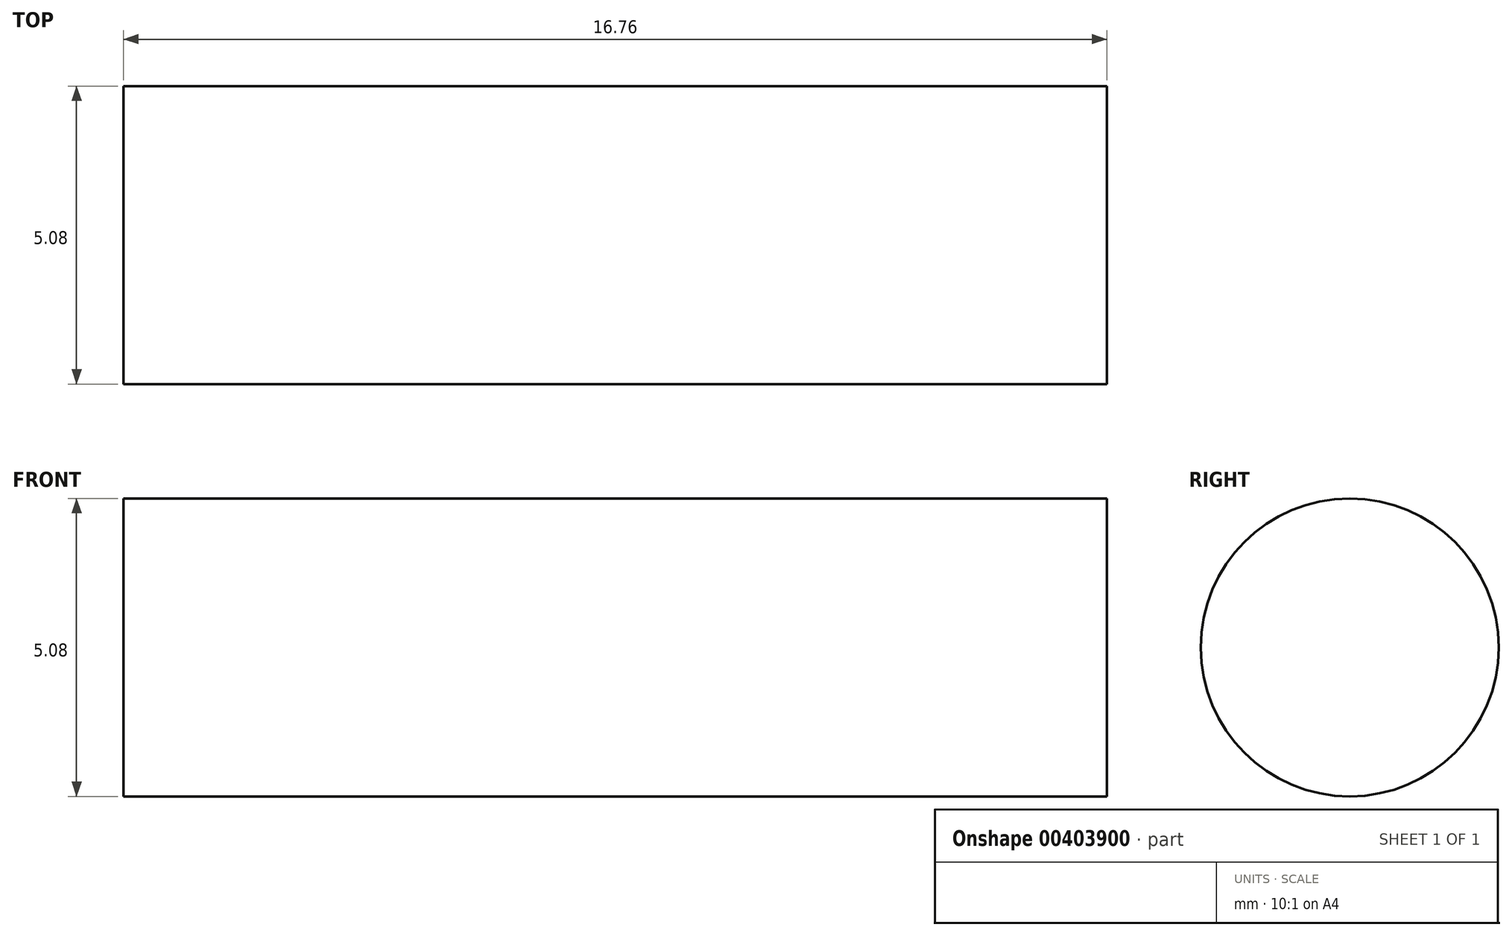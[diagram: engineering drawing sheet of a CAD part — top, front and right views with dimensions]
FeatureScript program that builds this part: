
annotation { "Feature Type Name" : "Feature", "Feature Type Description" : "" }
export const myFeature = defineFeature(function(context is Context, id is Id, definition is map)
    precondition{}
    {
        {
            var Q0;
            Q0=qCreatedBy(makeId("Right.planeOp"),FACE);
            var sketch = newSketch(context, id + "F0", { "sketchPlane" : qUnion([Q0])});
            skCircle(sketch, "E0", {"center": v(0, 0) * mm, "radius": 12.7 * mm});
            skSolve(sketch);
        }
        {
            var Q0;
            Q0=qSketchRegion(id+"F0",true);
            var Q1;
            Q1=makeQuery(id+"F0.imprint","IMPRINT",FACE,{"disambiguationData":[TD([[makeQuery(id+"F0.imprint","IMPRINT",EDGE,{"derivedFrom":sQuery(id+"F0.wireOp",EDGE,"E0")}),1.0]])]});
            extrude(context, id + "F1", {"entities" : qUnion([Q0, Q1]), "depth" : 83.82 * mm});
        }
        {
            var Q0;
            Q0=makeQuery(id+"F1.opExtrude","SWEPT_BODY",BODY,{"disambiguationData":[OSD([sQuery(id+"F0.wireOp",EDGE,"E0")])]});
            var Q1;
            Q1=qCreatedBy(makeId("Origin.pointOp"),VERTEX);
            transform(context, id + "F2", {"entities" : qUnion([Q0]), "transformType" : TransformType.SCALE_UNIFORMLY, "scale" : .2, "scalePoint" : qUnion([Q1]), "makeCopy" : false});
        }
    });
